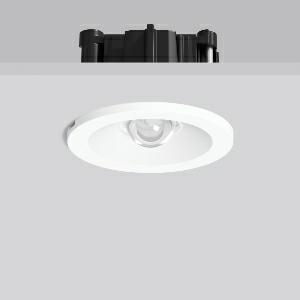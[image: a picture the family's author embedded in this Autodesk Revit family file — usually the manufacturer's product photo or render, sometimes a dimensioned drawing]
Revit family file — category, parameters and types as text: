
# Revit family: turia_l_672412_002_04_f3ce
name_source: partatom
category: Lighting Fixtures
units: mm (PartAtom-declared; Revit-internal decimal feet)

## family parameters
Cut with Voids When Loaded = No
Host = Face
Light Source = No
Part Type = Normal
Room Calculation Point = No
Round Connector Dimension = Use Diameter
Shared = No

## types (1)
- TURIA L (1 x LED Modul 765, 270 lm, 6500)
    Apparent Load = 5 VA
    CIE Flux Codes = 16 58 99 100 100
    Color Rendering = 70
    Color Temperature = 6500
    Default Elevation = 1800 mm
    Description = Series: TURIA L
Round emergency luminaire for escape route lighting. Housing: die-cast aluminium. Bezel ring: plastic. With plastic lenses for area lighting. Self-contained system with automatic self-test and feedback to the RZB monitoring system MULTIDIGIT. With enclosed separate ceiling mounting ring also suitable for ceiling cut-outs of Ø 68 mm. 
Colour: white
Diameter: 62 mm
Height: 3 mm
Cut-out diameter: 54-68 mm
Recess height: 76-162 mm
Luminaire: recess height: 42 mm
Weight: 430 g
Operating mode: maintained power mode
Duration time: 3 h
Lamp: LED
Socket: without socket
Colour temperature: 6500K
Colour rendering index (CRI): 70
System power: 5.3 W
Rated luminous flux: 270 lm
Luminous flux, emergency: 190 lm
System power, emergency: -
Control gear: Regulated power supply
Protection class: II
Type of protection: IP 20
    Height = 0 mm  [stored 0 ft]
    Lamp = 1 x LED Modul 765
    Lamp Light Flux = 270 lm
    Lamp count = 1
    Length = 62 mm  [stored 0.203412 ft]
    Lifetime = 50000 h
    Luminous efficacy = 51 lm/W
    Manufacturer = RZB
    ModVariant = No
    Model = 672412.002.04
    Mounting Place = Ceiling
    Mounting Type = Recessed
    Number of Poles = 1
    OnlyDefault = Yes
    Power Factor = 1
    Product Name = TURIA L
    Product group = Recessed ceiling luminaires
    ProductGroupID = 405
    Protection Class = Protection class II
    Protection Degree = IP 20
    RLX_Detail_Level = 1
    RLX_Emergency_Light_Flux = 190 lm
    RLX_Emergency_Type = 3
    RLX_Emergency_Type_DB = Yes
    RlxData = <blob elided: 35809 chars, md5=0a513f19>
    Socket = socket
    Standby Power = 0 W
    System Light Flux = 270 lm
    System Power = 5 W
    Type Comments = Product without accessories
    Type Image = 672412.002.jpg
    URL = http://relux.com
    VarID = ---
    Voltage = 230 V
    Voltage Range = 220-240 V
    Weight = 0.00 kg
    Width = 0 mm  [stored 0 ft]

note: [stored X ft] marks values corroborated as IEEE doubles in the binary element streams (Revit-internal decimal feet)

## geometry (parser evidence)
native form markers: Blend x4, Sweep x12
no freeform markers — native parametric forms only
